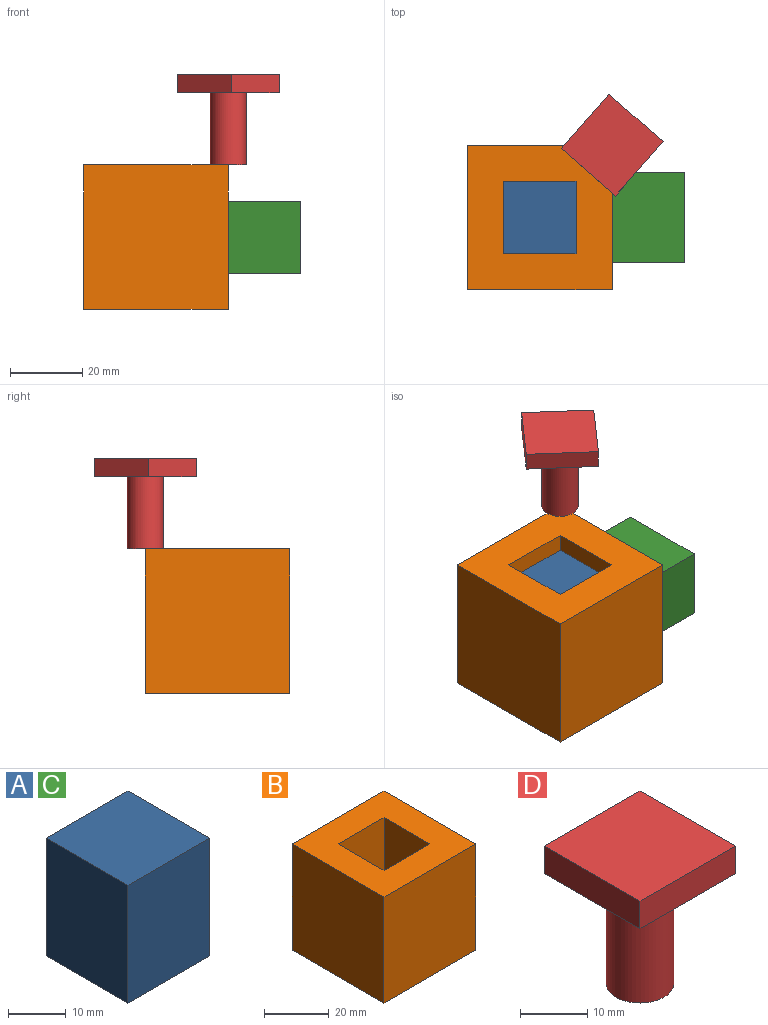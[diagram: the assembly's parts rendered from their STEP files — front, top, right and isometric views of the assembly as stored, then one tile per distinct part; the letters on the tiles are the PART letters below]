
ASSEMBLY  parts=4 mates=3
PART A: 6 faces, bbox 20x20x25 mm
  f0: plane 20x20mm, normal (0,0,-1), area 400mm2, adj f1,f2,f3,f4
  f1: plane 25x20mm, normal (1,0,0), area 500mm2, adj f0,f2,f4,f5
  f2: plane 25x20mm, normal (0,1,0), area 500mm2, adj f0,f1,f3,f5
  f3: plane 25x20mm, normal (-1,0,0), area 500mm2, adj f0,f2,f4,f5
  f4: plane 25x20mm, normal (0,-1,0), area 500mm2, adj f0,f1,f3,f5
  f5: plane 20x20mm, normal (0,0,1), area 400mm2, adj f1,f2,f3,f4
PART B: 11 faces, bbox 40x40x40 mm
  f0: plane 40x40mm, normal (0,0,1), area 1200mm2, adj f1,f2,f3,f4,f6,f7,f8,f9
  f1: plane 40x40mm, normal (1,0,0), area 1600mm2, adj f0,f2,f4,f5
  f2: plane 40x40mm, normal (0,1,0), area 1600mm2, adj f0,f1,f3,f5
  f3: plane 40x40mm, normal (-1,0,0), area 1600mm2, adj f0,f2,f4,f5
  f4: plane 40x40mm, normal (0,-1,0), area 1600mm2, adj f0,f1,f3,f5
  f5: plane 40x40mm, normal (0,0,-1), area 1600mm2, adj f1,f2,f3,f4
  f6: plane 30x20mm, normal (-1,0,0), area 600mm2, adj f0,f7,f9,f10
  f7: plane 30x20mm, normal (0,-1,0), area 600mm2, adj f0,f6,f8,f10
  f8: plane 30x20mm, normal (1,0,0), area 600mm2, adj f0,f7,f9,f10
  f9: plane 30x20mm, normal (0,1,0), area 600mm2, adj f0,f6,f8,f10
  f10: plane 20x20mm, normal (0,0,1), area 400mm2, adj f6,f7,f8,f9
PART C: same geometry as A
PART D: 8 faces, bbox 20x20x25 mm
  f0: cylinder r=5mm len=20mm, axis (0,0,-1), area 628.3mm2, adj f1,f6
  f1: plane 10x10mm, normal (0,0,-1), area 78.5mm2, adj f0
  f2: plane 20x5mm, normal (0,-1,0), area 100mm2, adj f3,f5,f6,f7
  f3: plane 20x5mm, normal (1,0,0), area 100mm2, adj f2,f4,f6,f7
  f4: plane 20x5mm, normal (0,1,0), area 100mm2, adj f3,f5,f6,f7
  f5: plane 20x5mm, normal (-1,0,0), area 100mm2, adj f2,f4,f6,f7
  f6: plane 20x20mm, normal (0,0,-1), area 321.5mm2, adj f0,f2,f3,f4,f5
  f7: plane 20x20mm, normal (0,0,1), area 400mm2, adj f2,f3,f4,f5
PLACE A at identity
PLACE B at identity fixed
PLACE C rot(axis=(-1,0,0),90deg) t=(30,17.5,-20)mm
PLACE D rot(axis=(0,0,-1),131.3deg) t=(20,20,0)mm
MATE revolute B.f0 <-> D.f0  axis (0,0,1) through (20,20,0)mm
MATE fastened B.f1 <-> C.f3  axis (1,0,0) through (20,0,-20)mm
MATE slider A.f0 <-> B.f10  axis (0,0,1) through (-10,10,-30)mm
